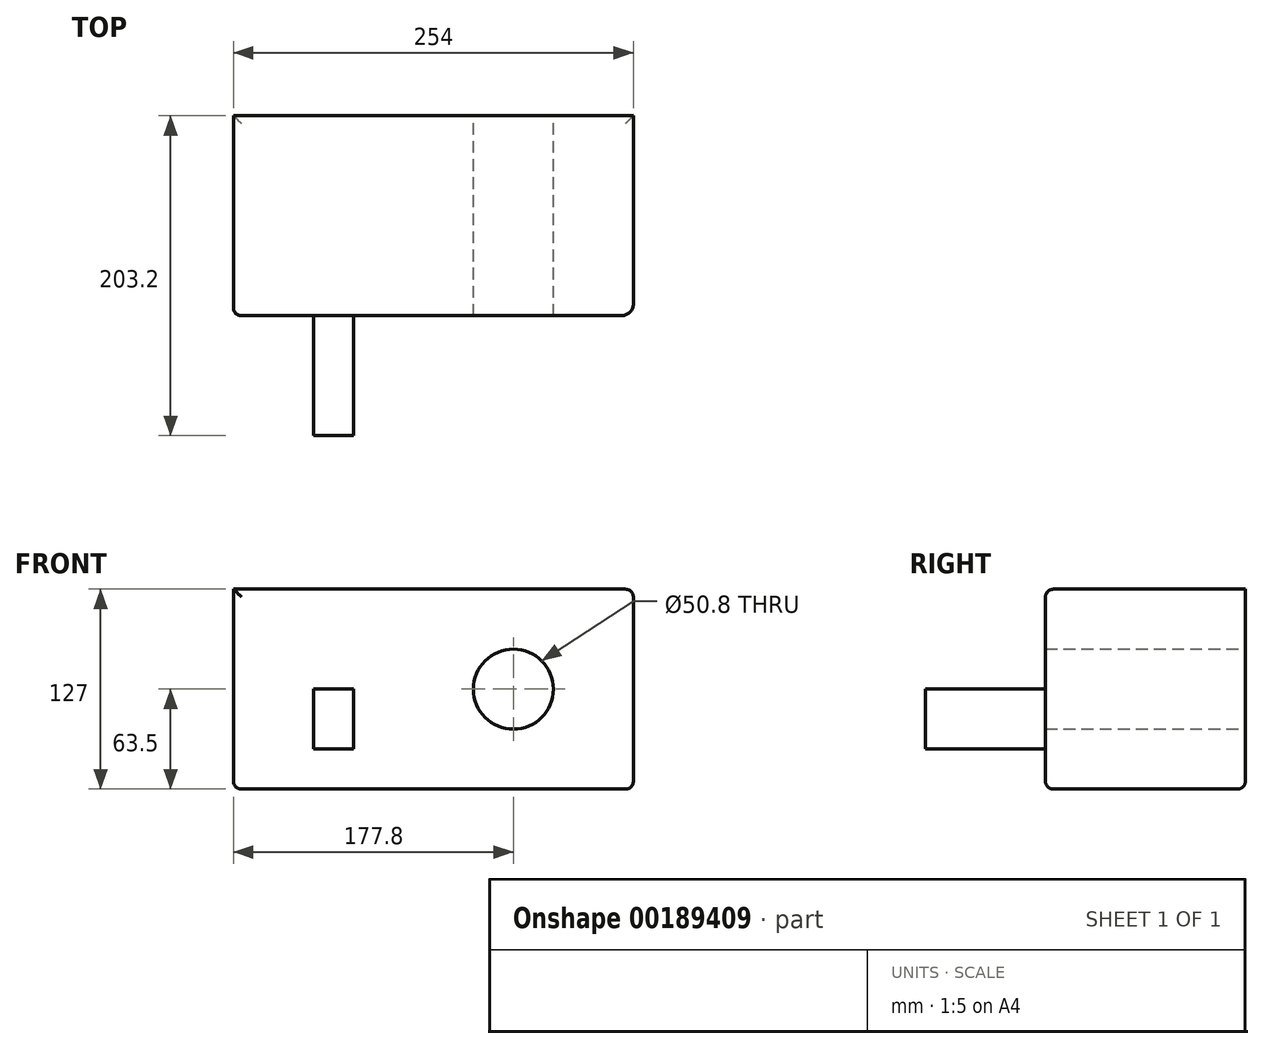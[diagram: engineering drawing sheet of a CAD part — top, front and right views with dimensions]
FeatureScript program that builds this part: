
annotation { "Feature Type Name" : "Feature", "Feature Type Description" : "" }
export const myFeature = defineFeature(function(context is Context, id is Id, definition is map)
    precondition{}
    {
        {
            var Q0;
            Q0=qCreatedBy(makeId("Front.planeOp"),FACE);
            var sketch = newSketch(context, id + "F0", { "sketchPlane" : qUnion([Q0])});
            skLineSegment(sketch, "E0.bottom", {"start": v(0, 0) * mm, "end": v(254, 0) * mm});
            skLineSegment(sketch, "E0.top", {"start": v(0, 127) * mm, "end": v(254, 127) * mm});
            skLineSegment(sketch, "E0.left", {"start": v(0, 0) * mm, "end": v(0, 127) * mm});
            skLineSegment(sketch, "E0.right", {"start": v(254, 0) * mm, "end": v(254, 127) * mm});
            skCircle(sketch, "E1", {"center": v(177.8, 63.5) * mm, "radius": 25.4 * mm});
            skSolve(sketch);
        }
        {
            var Q0;
            Q0 = qSketchRegion(id + "F0", true);
            extrude(context, id + "F1", {"entities" : qUnion([Q0]), "depth" : 127 * mm});
        }
        {
            var Q0;
            Q0=makeQuery(id+"F1.opExtrude","CAP_FACE",FACE,{"disambiguationData":[OSD([sQuery(id+"F0.wireOp",EDGE,"E0.bottom"),sQuery(id+"F0.wireOp",EDGE,"E0.top"),sQuery(id+"F0.wireOp",EDGE,"E0.left"),sQuery(id+"F0.wireOp",EDGE,"E0.right"),sQuery(id+"F0.wireOp",EDGE,"E1")])],"isStart":false});
            var sketch = newSketch(context, id + "F2", { "sketchPlane" : qUnion([Q0])});
            skLineSegment(sketch, "E2.bottom", {"start": v(50.8, 63.5) * mm, "end": v(76.2, 63.5) * mm});
            skLineSegment(sketch, "E2.top", {"start": v(50.8, 25.4) * mm, "end": v(76.2, 25.4) * mm});
            skLineSegment(sketch, "E2.left", {"start": v(50.8, 63.5) * mm, "end": v(50.8, 25.4) * mm});
            skLineSegment(sketch, "E2.right", {"start": v(76.2, 63.5) * mm, "end": v(76.2, 25.4) * mm});
            skSolve(sketch);
        }
        {
            var Q0;
            Q0 = qSketchRegion(id + "F2", true);
            extrude(context, id + "F3", {"entities" : qUnion([Q0]), "operationType" : NewBodyOperationType.ADD, "depth" : 76.2 * mm});
        }
        {
            var Q0;
            Q0=makeQuery(id+"F1.opExtrude","CAP_EDGE",EDGE,{"disambiguationData":[OSD([sQuery(id+"F0.wireOp",EDGE,"E0.right")])],"isStart":false});
            fillet(context, id + "F4", {"entities" : qUnion([Q0]), "radius" : 7.62 * mm, "tangentPropagation" : true, "allowEdgeOverflow" : false});
        }
        {
            var Q0;
            Q0=makeQuery(id+"F1.opExtrude","SWEPT_FACE",FACE,{"disambiguationData":[OSD([sQuery(id+"F0.wireOp",EDGE,"E0.bottom")])]});
            var Q1;
            Q1=makeQuery(id+"F1.opExtrude","CAP_EDGE",EDGE,{"disambiguationData":[OSD([sQuery(id+"F0.wireOp",EDGE,"E0.left")])],"isStart":false});
            var Q2;
            Q2=makeQuery(id+"F1.opExtrude","CAP_EDGE",EDGE,{"disambiguationData":[OSD([sQuery(id+"F0.wireOp",EDGE,"E0.top")])],"isStart":false});
            fillet(context, id + "F5", {"entities" : qUnion([Q0, Q1, Q2]), "radius" : 5.08 * mm, "tangentPropagation" : true, "allowEdgeOverflow" : false});
        }
    });
